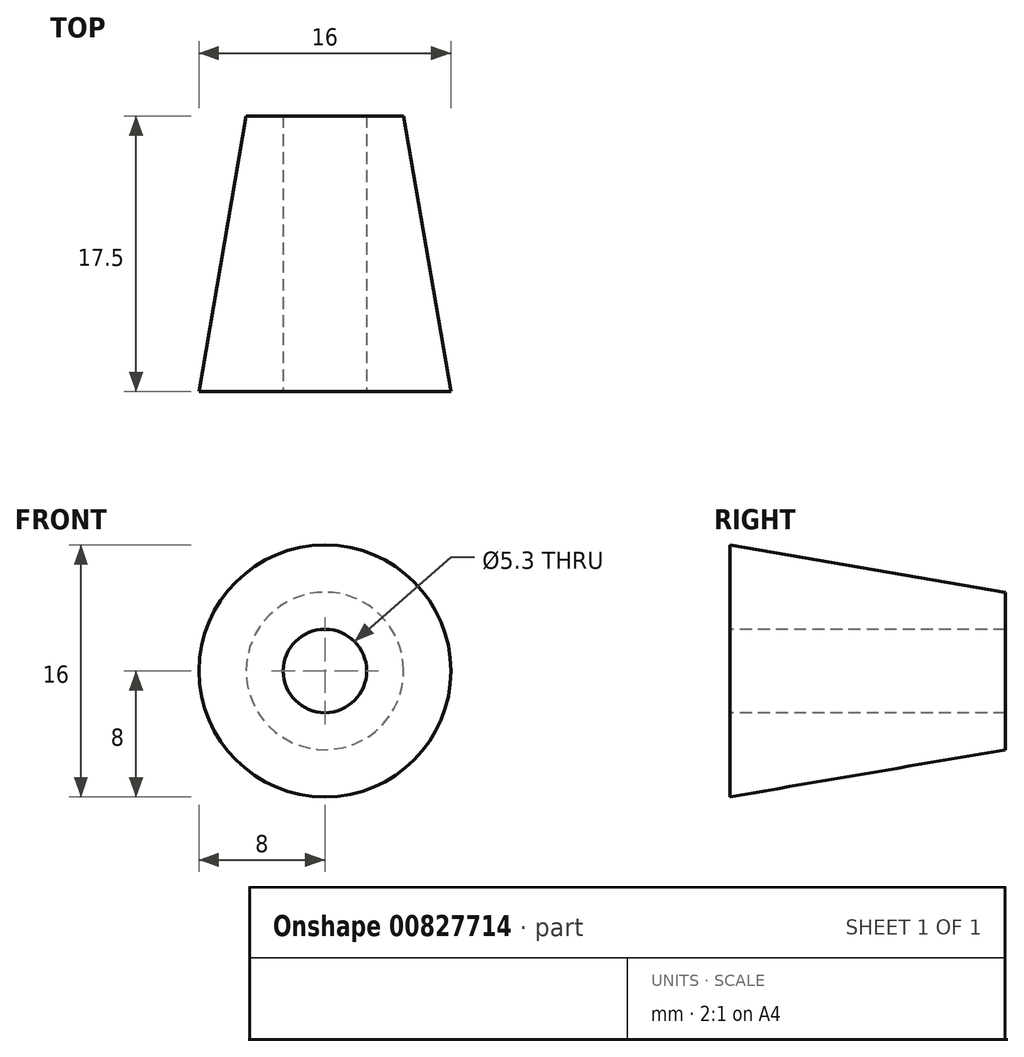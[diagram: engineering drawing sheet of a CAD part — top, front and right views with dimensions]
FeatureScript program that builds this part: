
annotation { "Feature Type Name" : "Feature", "Feature Type Description" : "" }
export const myFeature = defineFeature(function(context is Context, id is Id, definition is map)
    precondition{}
    {
        {
            var Q0;
            Q0=qCreatedBy(makeId("Front.planeOp"),FACE);
            var sketch = newSketch(context, id + "F0", { "sketchPlane" : qUnion([Q0])});
            skCircle(sketch, "E0", {"center": v(0, 0) * mm, "radius": 5 * mm});
            skLineSegment(sketch, "E1", {"start": v(0, 0) * mm, "end": v(0, -5) * mm});
            skSolve(sketch);
        }
        {
            var Q0;
            Q0=qCreatedBy(makeId("Front.planeOp"),FACE);
            cPlane(context, id + "F1", {"entities" : qUnion([Q0]), "cplaneType" : CPlaneType.OFFSET, "offset" : 17.5 * mm, "width" : 150 * mm, "height" : 150 * mm});
        }
        {
            var Q0;
            Q0=qCreatedBy(id+"F1.planeOp",FACE);
            var sketch = newSketch(context, id + "F2", { "sketchPlane" : qUnion([Q0])});
            skCircle(sketch, "E2", {"center": v(0, 0) * mm, "radius": 8 * mm});
            skSolve(sketch);
        }
        {
            var Q0;
            Q0=makeQuery(id+"F2.imprint","IMPRINT",FACE,{"disambiguationData":[TD([[makeQuery(id+"F2.imprint","IMPRINT",EDGE,{"derivedFrom":sQuery(id+"F2.wireOp",EDGE,"E2")}),1.0]])]});
            var Q1;
            Q1=makeQuery(id+"F0.imprint","IMPRINT",FACE,{"disambiguationData":[TD([[makeQuery(id+"F0.imprint","IMPRINT",EDGE,{"derivedFrom":sQuery(id+"F0.wireOp",EDGE,"E0")}),1.0]])]});
            loft(context, id + "F3", {"sheetProfilesArray" : [{ "sheetProfileEntities" : qUnion([Q0]) }, { "sheetProfileEntities" : qUnion([Q1]) }]});
        }
        {
            var Q0;
            Q0=sQuery(id+"F0.wireOp",VERTEX,"E1.start");
            var Q1;
            Q1=makeQuery(id+"F3.opLoft","SWEPT_BODY",BODY,{"disambiguationData":[OSD([makeQuery(id+"F0.imprint","IMPRINT",FACE,{"disambiguationData":[TD([[makeQuery(id+"F0.imprint","IMPRINT",EDGE,{"derivedFrom":sQuery(id+"F0.wireOp",EDGE,"E0")}),1.0]])]}),makeQuery(id+"F2.imprint","IMPRINT",FACE,{"disambiguationData":[TD([[makeQuery(id+"F2.imprint","IMPRINT",EDGE,{"derivedFrom":sQuery(id+"F2.wireOp",EDGE,"E2")}),1.0]])]})])]});
            hole(context, id + "F4", {"style" : HoleStyle.SIMPLE, "endStyle" : HoleEndStyle.THROUGH, "oppositeDirection" : true, "holeDiameter" : 5.3 * mm, "majorDiameter" : 5 * mm, "isTappedThrough" : true, "tappedDepth" : 12 * mm, "tapClearance" : 3, "locations" : qUnion([Q0]), "scope" : qUnion([Q1]), "startStyle" : HoleStartStyle.PART});
        }
    });
